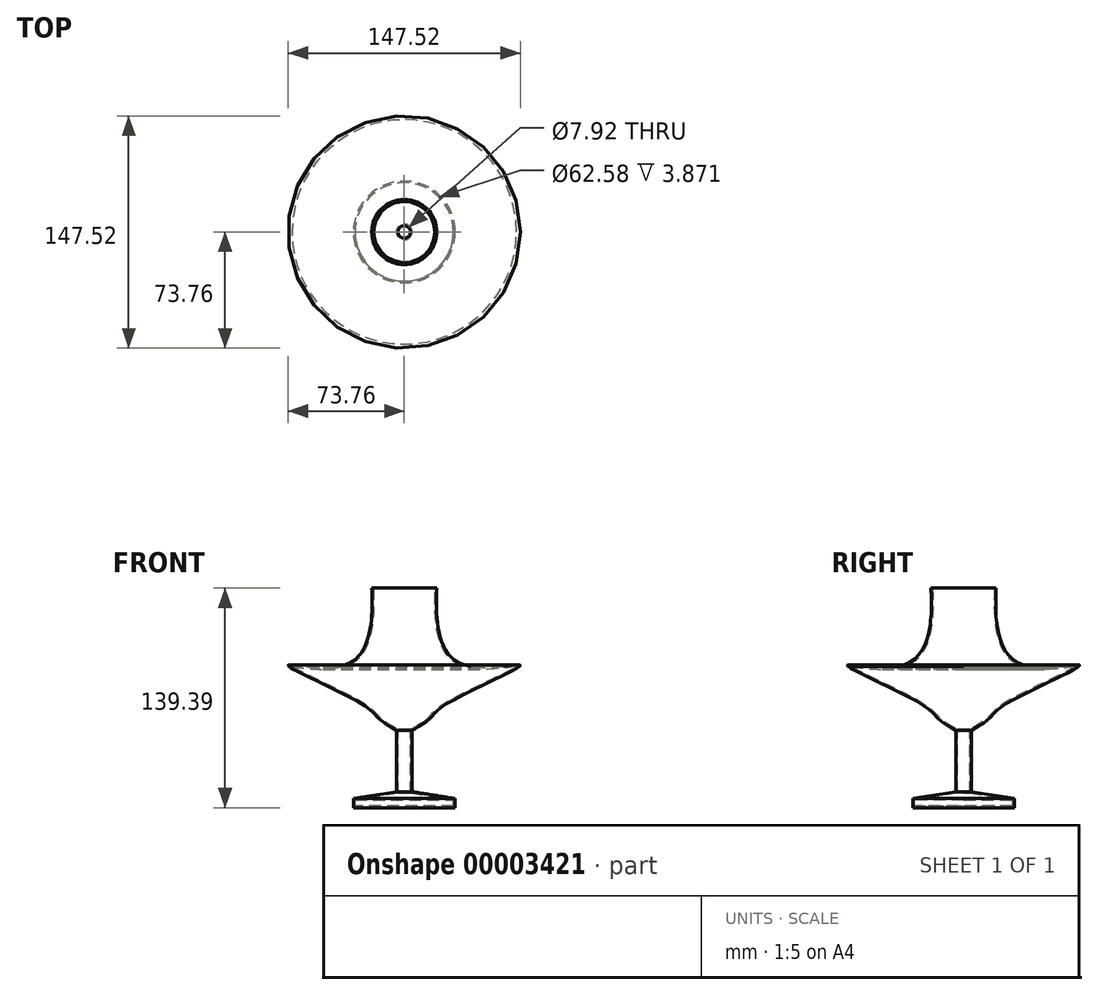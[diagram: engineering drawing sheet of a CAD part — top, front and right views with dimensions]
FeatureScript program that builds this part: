
annotation { "Feature Type Name" : "Feature", "Feature Type Description" : "" }
export const myFeature = defineFeature(function(context is Context, id is Id, definition is map)
    precondition{}
    {
        {
            var Q0;
            Q0=qCreatedBy(makeId("Front.planeOp"),FACE);
            var sketch = newSketch(context, id + "F0", { "sketchPlane" : qUnion([Q0])});
            skLineSegment(sketch, "E0", {"start": v(0, 0) * mm, "end": v(-32.3, 0) * mm});
            skLineSegment(sketch, "E1", {"start": v(-32.3, 0) * mm, "end": v(-32.3, 5.72) * mm});
            skLineSegment(sketch, "E2", {"start": v(-32.3, 5.72) * mm, "end": v(-4.96, 10.13) * mm});
            skLineSegment(sketch, "E3", {"start": v(-4.96, 10.13) * mm, "end": v(-4.96, 49.07) * mm});
            skFitSpline(sketch, "E4", {"points": [v(-4.96, 49.07) * mm, v(-15.78, 56.1) * mm, v(-25.2, 64.84) * mm, v(-73.76, 90.42) * mm, v(-31.44, 93.99) * mm, v(-20.65, 139.4) * mm], "startDerivative": vector(-53.68, 33.72) * mm, "endDerivative": vector(1.1, 45.51) * mm});
            skLineSegment(sketch, "E5", {"start": v(-20.65, 139.4) * mm, "end": v(0, 139.4) * mm});
            skLineSegment(sketch, "E6", {"start": v(0, 139.4) * mm, "end": v(0, 0) * mm});
            skSolve(sketch);
        }
        {
            var Q0;
            Q0 = qSketchRegion(id + "F0", true);
            var Q1;
            Q1=sQuery(id+"F0.wireOp",EDGE,"E6");
            revolve(context, id + "F1", {"entities" : qUnion([Q0]), "axis" : qUnion([Q1]), "revolveType" : RevolveType.FULL});
        }
        {
            var Q0;
            Q0=makeQuery(id+"F1.opRevolve","SWEPT_FACE",FACE,{"disambiguationData":[OSD([sQuery(id+"F0.wireOp",EDGE,"E5")])]});
            shell(context, id + "F2", {"entities" : qUnion([Q0]), "thickness" : 1 * mm});
        }
    });
